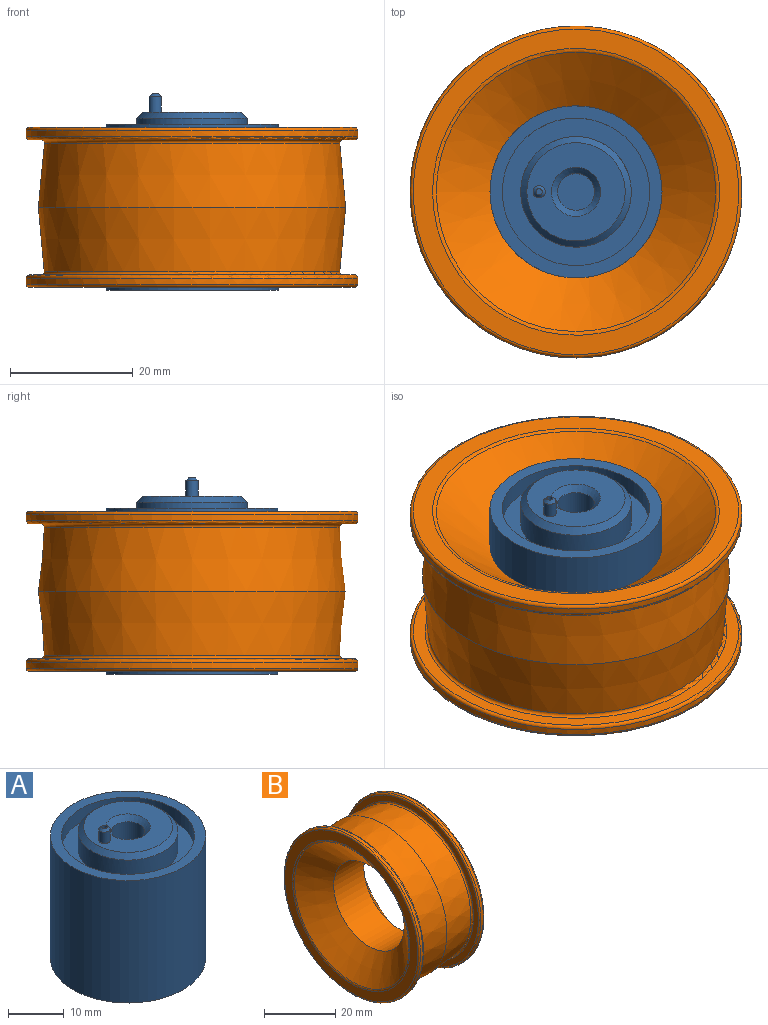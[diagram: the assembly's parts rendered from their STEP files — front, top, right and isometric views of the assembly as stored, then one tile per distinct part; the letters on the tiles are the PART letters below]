
ASSEMBLY  parts=2 mates=1
PART A: 17 faces, bbox 28x28x32 mm
  f0: plane 16x16mm, normal (0,0,1), area 147.7mm2, adj f11,f12,f14
  f1: plane 24x24mm, normal (0,0,-1), area 452.4mm2, adj f2
  f2: cylinder r=12mm len=24mm, axis (0,0,1), area 150.8mm2, adj f1,f3
  f3: plane 28x28mm, normal (0,0,-1), area 163.4mm2, adj f2,f4
  f4: cylinder r=14mm len=28mm, axis (0,0,1), area 2375mm2, adj f3,f5
  f5: plane 28x28mm, normal (0,0,1), area 163.4mm2, adj f4,f6
  f6: cylinder r=12mm len=24mm, axis (0,0,1), area 226.2mm2, adj f5,f7
  f7: plane 24x24mm, normal (0,0,1), area 197.9mm2, adj f6,f8
  f8: cylinder r=9mm len=18mm, axis (0,0,1), area 226.2mm2, adj f7,f12
  f9: cylinder r=3mm len=19mm, axis (0,0,1), area 358.1mm2, adj f10,f11
  f10: plane 6x6mm, normal (0,0,1), area 28.3mm2, adj f9
  f11: cone r=3mm half-angle=45deg, axis (0,0,1), area 31.1mm2, adj f0,f9
  f12: cone r=8mm half-angle=45deg, axis (0,0,-1), area 75.5mm2, adj f0,f8
  f13: cylinder r=0.5mm len=3mm, axis (0,0,-1), area 9.4mm2, adj f15,f16
  f14: cylinder r=1mm len=2.5mm, axis (0,0,-1), area 15.7mm2, adj f0,f16
  f15: plane 1x1mm, normal (0,0,1), area 0.8mm2, adj f13
  f16: cone r=0.5mm half-angle=45deg, axis (0,0,-1), area 3.3mm2, adj f13,f14
PART B: 19 faces, bbox 26x58.4x58.4 mm
  f0: cylinder r=14mm len=28mm, axis (-1,0,0), area 1055.6mm2, adj f1,f10
  f1: cone r=14mm half-angle=52.1deg, axis (1,0,0), area 1276mm2, adj f0,f17
  f2: plane 53x53mm, normal (1,0,0), area 494.3mm2, adj f11,f17
  f3: cylinder r=27mm len=54mm, axis (-1,0,0), area 169.6mm2, adj f11,f12
  f4: plane 53x53mm, normal (-1,0,0), area 313.1mm2, adj f12,f13
  f5: cone r=24mm half-angle=5.2deg, axis (-1,0,0), area 1617.7mm2, adj f6,f13
  f6: cone r=24mm half-angle=5.2deg, axis (1,0,0), area 1617.7mm2, adj f5,f14
  f7: plane 53x53mm, normal (1,0,0), area 313.1mm2, adj f14,f15
  f8: cylinder r=27mm len=54mm, axis (-1,0,0), area 169.6mm2, adj f15,f16
  f9: plane 53x53mm, normal (-1,0,0), area 494.3mm2, adj f16,f18
  f10: cone r=14mm half-angle=52.1deg, axis (-1,0,0), area 1276mm2, adj f0,f18
  f11: torus R=26.5mm, axis (-1,0,0), area 132.3mm2, adj f2,f3
  f12: torus R=26.5mm, axis (1,0,0), area 132.3mm2, adj f3,f4
  f13: torus R=24.55mm, axis (1,0,0), area 126.4mm2, adj f4,f5
  f14: torus R=24.55mm, axis (1,0,0), area 126.4mm2, adj f6,f7
  f15: torus R=26.5mm, axis (1,0,0), area 132.3mm2, adj f7,f8
  f16: torus R=26.5mm, axis (-1,0,0), area 132.3mm2, adj f8,f9
  f17: torus R=23.34mm, axis (-1,0,0), area 95.6mm2, adj f1,f2
  f18: torus R=23.34mm, axis (-1,0,0), area 95.6mm2, adj f9,f10
PLACE A t=(-11.03,-11.33,-0.03)mm
PLACE B rot(axis=(0.71,0,-0.71),180deg) t=(-11.03,-11.33,-2.03)mm
MATE fastened B.f0 <-> A.f2  axis (0,0,1) through (-11.03,-11.33,-2.03)mm
